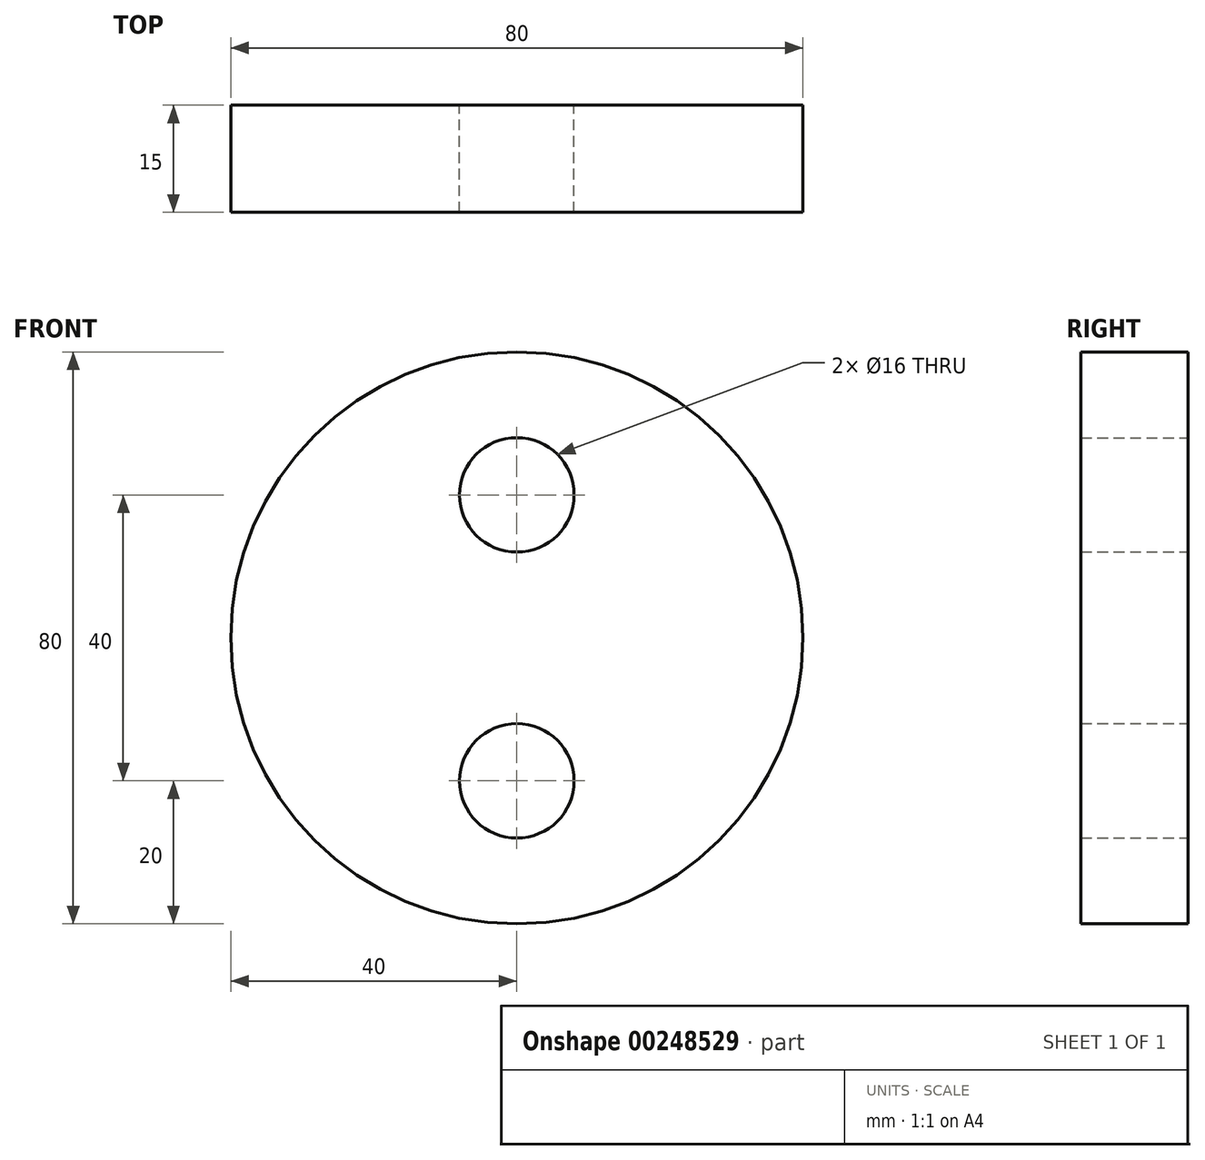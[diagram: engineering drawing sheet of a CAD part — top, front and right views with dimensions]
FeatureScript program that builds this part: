
annotation { "Feature Type Name" : "Feature", "Feature Type Description" : "" }
export const myFeature = defineFeature(function(context is Context, id is Id, definition is map)
    precondition{}
    {
        {
            var Q0;
            Q0=qCreatedBy(makeId("Front.planeOp"),FACE);
            var sketch = newSketch(context, id + "F0", { "sketchPlane" : qUnion([Q0])});
            skCircle(sketch, "E0", {"center": v(0, 0) * mm, "radius": 40 * mm});
            skArc(sketch, "E1", {"start": v(0, 40) * mm, "mid": v(-20, 20) * mm, "end": v(0, 0) * mm});
            skArc(sketch, "E2", {"start": v(0, -40) * mm, "mid": v(20, -20) * mm, "end": v(0, 0) * mm});
            skCircle(sketch, "E3", {"center": v(0, 20) * mm, "radius": 8 * mm});
            skCircle(sketch, "E4", {"center": v(0, -20) * mm, "radius": 8 * mm});
            skSolve(sketch);
        }
        {
            var Q0;
            Q0 = qSketchRegion(id + "F0", true);
            extrude(context, id + "F1", {"entities" : qUnion([Q0]), "endBound" : BoundingType.SYMMETRIC, "depth" : 15 * mm});
        }
        {
            var Q0;
            Q0=sQuery(id+"F0.wireOp",EDGE,"E1");
            var Q1;
            Q1=sQuery(id+"F0.wireOp",EDGE,"E2");
            var Q2;
            Q2=sQuery(id+"F0.wireOp",EDGE,"E3");
            var Q3;
            Q3=sQuery(id+"F0.wireOp",EDGE,"E4");
            extrude(context, id + "F2", {"bodyType" : ToolBodyType.SURFACE, "surfaceEntities" : qUnion([Q0, Q1, Q2, Q3]), "depth" : 8 * mm});
        }
    });
